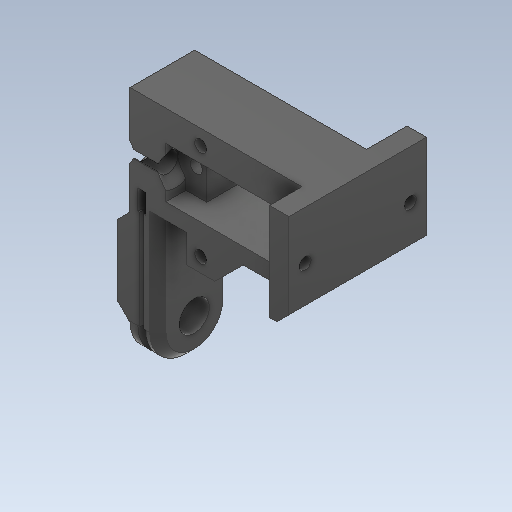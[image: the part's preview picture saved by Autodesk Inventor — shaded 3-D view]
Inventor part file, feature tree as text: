
AUTODESK INVENTOR PART (.ipt)
format: ipt  version: 2020 (Build 240168000, 168)  size: 465,408 bytes
history: native  units: in
note: dims shown in document units (in); Inventor stores cm internally (conversion verified against a paired STEP export)
features: sketch x35, other x3, plane x1
ambient origin geometry x8: Origin, YZ Plane, XZ Plane, XY Plane, X Axis, Y Axis, Z Axis, Center Point
bodies: Solid1 (feature_tree)
feature tree (39):
  other  "FermurSupport.ipt"
  other  "Solid1::FermurSupport.ipt"
  other  "TaggingFeature1"
  sketch  "Sketch1"  dims[d0=0.3937in]
  sketch  "Sketch2"
  sketch  "Sketch3"
  sketch  "Sketch4"
  sketch  "Sketch5"
  sketch  "Sketch6"
  sketch  "Sketch8"
  sketch  "Sketch10"
  sketch  "Sketch11"
  sketch  "Sketch12"
  sketch  "Sketch13"
  sketch  "Sketch14"
  sketch  "Sketch15"
  sketch  "Sketch17"
  sketch  "Sketch19"
  sketch  "Sketch21"
  sketch  "Sketch22"
  sketch  "Sketch23"
  sketch  "Sketch26"
  sketch  "Sketch27"
  sketch  "Sketch29"
  sketch  "Sketch32"
  sketch  "Sketch33"
  sketch  "Sketch36"
  sketch  "Sketch37"
  sketch  "Sketch38"
  sketch  "Sketch39"
  sketch  "Sketch41"
  sketch  "Sketch42"
  sketch  "Sketch43"
  sketch  "Sketch44"
  sketch  "Sketch45"
  sketch  "Sketch46"
  sketch  "Sketch47"
  sketch  "Sketch48"
  plane  "Work Plane1"
